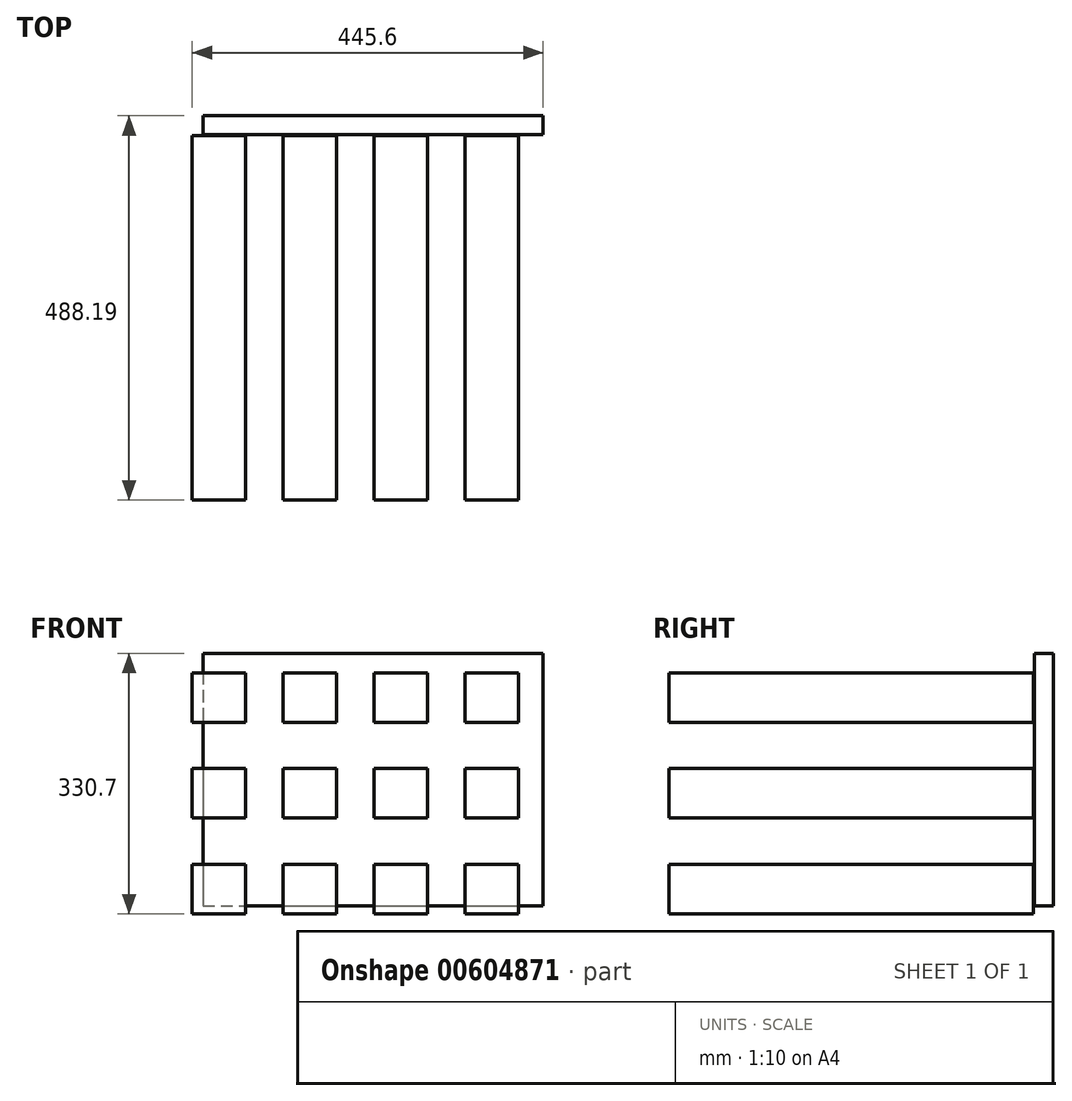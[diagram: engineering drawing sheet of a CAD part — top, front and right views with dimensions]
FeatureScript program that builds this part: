
annotation { "Feature Type Name" : "Feature", "Feature Type Description" : "" }
export const myFeature = defineFeature(function(context is Context, id is Id, definition is map)
    precondition{}
    {
        {
            var Q0;
            Q0=qCreatedBy(makeId("Front.planeOp"),FACE);
            var sketch = newSketch(context, id + "F0", { "sketchPlane" : qUnion([Q0])});
            skLineSegment(sketch, "E0.bottom", {"start": v(-32.14, 30.24) * mm, "end": v(35.66, 30.24) * mm});
            skLineSegment(sketch, "E0.top", {"start": v(-32.14, -32.68) * mm, "end": v(35.66, -32.68) * mm});
            skLineSegment(sketch, "E0.left", {"start": v(-32.14, 30.24) * mm, "end": v(-32.14, -32.68) * mm});
            skLineSegment(sketch, "E0.right", {"start": v(35.66, 30.24) * mm, "end": v(35.66, -32.68) * mm});
            skLineSegment(sketch, "E1.0.1.0", {"start": v(-32.14, 88.98) * mm, "end": v(35.66, 88.98) * mm});
            skLineSegment(sketch, "E1.0.1.1", {"start": v(-32.14, 151.9) * mm, "end": v(-32.14, 88.98) * mm});
            skLineSegment(sketch, "E1.0.1.2", {"start": v(35.66, 151.9) * mm, "end": v(35.66, 88.98) * mm});
            skLineSegment(sketch, "E1.0.1.3", {"start": v(-32.14, 151.9) * mm, "end": v(35.66, 151.9) * mm});
            skLineSegment(sketch, "E1.0.2.0", {"start": v(-32.14, 210.65) * mm, "end": v(35.66, 210.65) * mm});
            skLineSegment(sketch, "E1.0.2.1", {"start": v(-32.14, 273.57) * mm, "end": v(-32.14, 210.65) * mm});
            skLineSegment(sketch, "E1.0.2.2", {"start": v(35.66, 273.57) * mm, "end": v(35.66, 210.65) * mm});
            skLineSegment(sketch, "E1.0.2.3", {"start": v(-32.14, 273.57) * mm, "end": v(35.66, 273.57) * mm});
            skLineSegment(sketch, "E1.1.0.0", {"start": v(83.43, -32.68) * mm, "end": v(151.23, -32.68) * mm});
            skLineSegment(sketch, "E1.1.0.1", {"start": v(83.43, 30.24) * mm, "end": v(83.43, -32.68) * mm});
            skLineSegment(sketch, "E1.1.0.2", {"start": v(151.23, 30.24) * mm, "end": v(151.23, -32.68) * mm});
            skLineSegment(sketch, "E1.1.0.3", {"start": v(83.43, 30.24) * mm, "end": v(151.23, 30.24) * mm});
            skLineSegment(sketch, "E1.1.1.0", {"start": v(83.43, 88.98) * mm, "end": v(151.23, 88.98) * mm});
            skLineSegment(sketch, "E1.1.1.1", {"start": v(83.43, 151.9) * mm, "end": v(83.43, 88.98) * mm});
            skLineSegment(sketch, "E1.1.1.2", {"start": v(151.23, 151.9) * mm, "end": v(151.23, 88.98) * mm});
            skLineSegment(sketch, "E1.1.1.3", {"start": v(83.43, 151.9) * mm, "end": v(151.23, 151.9) * mm});
            skLineSegment(sketch, "E1.1.2.0", {"start": v(83.43, 210.65) * mm, "end": v(151.23, 210.65) * mm});
            skLineSegment(sketch, "E1.1.2.1", {"start": v(83.43, 273.57) * mm, "end": v(83.43, 210.65) * mm});
            skLineSegment(sketch, "E1.1.2.2", {"start": v(151.23, 273.57) * mm, "end": v(151.23, 210.65) * mm});
            skLineSegment(sketch, "E1.1.2.3", {"start": v(83.43, 273.57) * mm, "end": v(151.23, 273.57) * mm});
            skLineSegment(sketch, "E1.2.0.0", {"start": v(199, -32.68) * mm, "end": v(266.8, -32.68) * mm});
            skLineSegment(sketch, "E1.2.0.1", {"start": v(199, 30.24) * mm, "end": v(199, -32.68) * mm});
            skLineSegment(sketch, "E1.2.0.2", {"start": v(266.8, 30.24) * mm, "end": v(266.8, -32.68) * mm});
            skLineSegment(sketch, "E1.2.0.3", {"start": v(199, 30.24) * mm, "end": v(266.8, 30.24) * mm});
            skLineSegment(sketch, "E1.2.1.0", {"start": v(199, 88.98) * mm, "end": v(266.8, 88.98) * mm});
            skLineSegment(sketch, "E1.2.1.1", {"start": v(199, 151.9) * mm, "end": v(199, 88.98) * mm});
            skLineSegment(sketch, "E1.2.1.2", {"start": v(266.8, 151.9) * mm, "end": v(266.8, 88.98) * mm});
            skLineSegment(sketch, "E1.2.1.3", {"start": v(199, 151.9) * mm, "end": v(266.8, 151.9) * mm});
            skLineSegment(sketch, "E1.2.2.0", {"start": v(199, 210.65) * mm, "end": v(266.8, 210.65) * mm});
            skLineSegment(sketch, "E1.2.2.1", {"start": v(199, 273.57) * mm, "end": v(199, 210.65) * mm});
            skLineSegment(sketch, "E1.2.2.2", {"start": v(266.8, 273.57) * mm, "end": v(266.8, 210.65) * mm});
            skLineSegment(sketch, "E1.2.2.3", {"start": v(199, 273.57) * mm, "end": v(266.8, 273.57) * mm});
            skLineSegment(sketch, "E1.3.0.0", {"start": v(314.57, -32.68) * mm, "end": v(382.37, -32.68) * mm});
            skLineSegment(sketch, "E1.3.0.1", {"start": v(314.57, 30.24) * mm, "end": v(314.57, -32.68) * mm});
            skLineSegment(sketch, "E1.3.0.2", {"start": v(382.37, 30.24) * mm, "end": v(382.37, -32.68) * mm});
            skLineSegment(sketch, "E1.3.0.3", {"start": v(314.57, 30.24) * mm, "end": v(382.37, 30.24) * mm});
            skLineSegment(sketch, "E1.3.1.0", {"start": v(314.57, 88.98) * mm, "end": v(382.37, 88.98) * mm});
            skLineSegment(sketch, "E1.3.1.1", {"start": v(314.57, 151.9) * mm, "end": v(314.57, 88.98) * mm});
            skLineSegment(sketch, "E1.3.1.2", {"start": v(382.37, 151.9) * mm, "end": v(382.37, 88.98) * mm});
            skLineSegment(sketch, "E1.3.1.3", {"start": v(314.57, 151.9) * mm, "end": v(382.37, 151.9) * mm});
            skLineSegment(sketch, "E1.3.2.0", {"start": v(314.57, 210.65) * mm, "end": v(382.37, 210.65) * mm});
            skLineSegment(sketch, "E1.3.2.1", {"start": v(314.57, 273.57) * mm, "end": v(314.57, 210.65) * mm});
            skLineSegment(sketch, "E1.3.2.2", {"start": v(382.37, 273.57) * mm, "end": v(382.37, 210.65) * mm});
            skLineSegment(sketch, "E1.3.2.3", {"start": v(314.57, 273.57) * mm, "end": v(382.37, 273.57) * mm});
            skLineSegment(sketch, "E1.direction1", {"start": v(-32.14, -32.68) * mm, "end": v(83.43, -32.68) * mm, "construction": true});
            skLineSegment(sketch, "E1.direction2", {"start": v(-32.14, -32.68) * mm, "end": v(-32.14, 88.98) * mm, "construction": true});
            skSolve(sketch);
        }
        {
            var Q0;
            Q0=makeQuery(id+"F0.imprint","IMPRINT",FACE,{"disambiguationData":[TD([[makeQuery(id+"F0.imprint","IMPRINT",EDGE,{"derivedFrom":sQuery(id+"F0.wireOp",EDGE,"E0.bottom")}),-1.0]])]});
            var Q1;
            Q1=makeQuery(id+"F0.imprint","IMPRINT",FACE,{"disambiguationData":[TD([[makeQuery(id+"F0.imprint","IMPRINT",EDGE,{"derivedFrom":sQuery(id+"F0.wireOp",EDGE,"E1.0.1.0")}),1.0]])]});
            var Q2;
            Q2=makeQuery(id+"F0.imprint","IMPRINT",FACE,{"disambiguationData":[TD([[makeQuery(id+"F0.imprint","IMPRINT",EDGE,{"derivedFrom":sQuery(id+"F0.wireOp",EDGE,"E1.0.2.0")}),1.0]])]});
            var Q3;
            Q3=makeQuery(id+"F0.imprint","IMPRINT",FACE,{"disambiguationData":[TD([[makeQuery(id+"F0.imprint","IMPRINT",EDGE,{"derivedFrom":sQuery(id+"F0.wireOp",EDGE,"E1.1.0.0")}),1.0]])]});
            var Q4;
            Q4=makeQuery(id+"F0.imprint","IMPRINT",FACE,{"disambiguationData":[TD([[makeQuery(id+"F0.imprint","IMPRINT",EDGE,{"derivedFrom":sQuery(id+"F0.wireOp",EDGE,"E1.1.1.0")}),1.0]])]});
            var Q5;
            Q5=makeQuery(id+"F0.imprint","IMPRINT",FACE,{"disambiguationData":[TD([[makeQuery(id+"F0.imprint","IMPRINT",EDGE,{"derivedFrom":sQuery(id+"F0.wireOp",EDGE,"E1.1.2.0")}),1.0]])]});
            var Q6;
            Q6=makeQuery(id+"F0.imprint","IMPRINT",FACE,{"disambiguationData":[TD([[makeQuery(id+"F0.imprint","IMPRINT",EDGE,{"derivedFrom":sQuery(id+"F0.wireOp",EDGE,"E1.2.0.0")}),1.0]])]});
            var Q7;
            Q7=makeQuery(id+"F0.imprint","IMPRINT",FACE,{"disambiguationData":[TD([[makeQuery(id+"F0.imprint","IMPRINT",EDGE,{"derivedFrom":sQuery(id+"F0.wireOp",EDGE,"E1.2.1.0")}),1.0]])]});
            var Q8;
            Q8=makeQuery(id+"F0.imprint","IMPRINT",FACE,{"disambiguationData":[TD([[makeQuery(id+"F0.imprint","IMPRINT",EDGE,{"derivedFrom":sQuery(id+"F0.wireOp",EDGE,"E1.2.2.0")}),1.0]])]});
            var Q9;
            Q9=makeQuery(id+"F0.imprint","IMPRINT",FACE,{"disambiguationData":[TD([[makeQuery(id+"F0.imprint","IMPRINT",EDGE,{"derivedFrom":sQuery(id+"F0.wireOp",EDGE,"E1.3.0.0")}),1.0]])]});
            var Q10;
            Q10=makeQuery(id+"F0.imprint","IMPRINT",FACE,{"disambiguationData":[TD([[makeQuery(id+"F0.imprint","IMPRINT",EDGE,{"derivedFrom":sQuery(id+"F0.wireOp",EDGE,"E1.3.1.0")}),1.0]])]});
            var Q11;
            Q11=makeQuery(id+"F0.imprint","IMPRINT",FACE,{"disambiguationData":[TD([[makeQuery(id+"F0.imprint","IMPRINT",EDGE,{"derivedFrom":sQuery(id+"F0.wireOp",EDGE,"E1.3.2.0")}),1.0]])]});
            extrude(context, id + "F1", {"entities" : qUnion([Q0, Q1, Q2, Q3, Q4, Q5, Q6, Q7, Q8, Q9, Q10, Q11]), "depth" : 462.8 * mm, "offsetDistance" : 25.4 * mm});
        }
        {
            var Q0;
            Q0=makeQuery(id+"F1.opExtrude","CAP_FACE",FACE,{"disambiguationData":[OSD([sQuery(id+"F0.wireOp",EDGE,"E1.1.1.0"),sQuery(id+"F0.wireOp",EDGE,"E1.1.1.1"),sQuery(id+"F0.wireOp",EDGE,"E1.1.1.2"),sQuery(id+"F0.wireOp",EDGE,"E1.1.1.3")])],"isStart":true});
            cPlane(context, id + "F2", {"entities" : qUnion([Q0]), "cplaneType" : CPlaneType.OFFSET, "offset" : 25.4 * mm, "width" : 152.4 * mm, "height" : 152.4 * mm});
        }
        {
            var Q0;
            Q0=qCreatedBy(id+"F2.planeOp",FACE);
            var sketch = newSketch(context, id + "F3", { "sketchPlane" : qUnion([Q0])});
            skLineSegment(sketch, "E2.bottom", {"start": v(18.54, 298.02) * mm, "end": v(-413.46, 298.02) * mm});
            skLineSegment(sketch, "E2.top", {"start": v(18.54, -22.54) * mm, "end": v(-413.46, -22.54) * mm});
            skLineSegment(sketch, "E2.left", {"start": v(18.54, 298.02) * mm, "end": v(18.54, -22.54) * mm});
            skLineSegment(sketch, "E2.right", {"start": v(-413.46, 298.02) * mm, "end": v(-413.46, -22.54) * mm});
            skSolve(sketch);
        }
        {
            var Q0;
            Q0=makeQuery(id+"F3.imprint","IMPRINT",FACE,{"disambiguationData":[TD([[makeQuery(id+"F3.imprint","IMPRINT",EDGE,{"derivedFrom":sQuery(id+"F3.wireOp",EDGE,"E2.bottom")}),1.0]])]});
            extrude(context, id + "F4", {"entities" : qUnion([Q0]), "oppositeDirection" : true, "depth" : 24.13 * mm, "offsetDistance" : 25.4 * mm});
        }
    });
